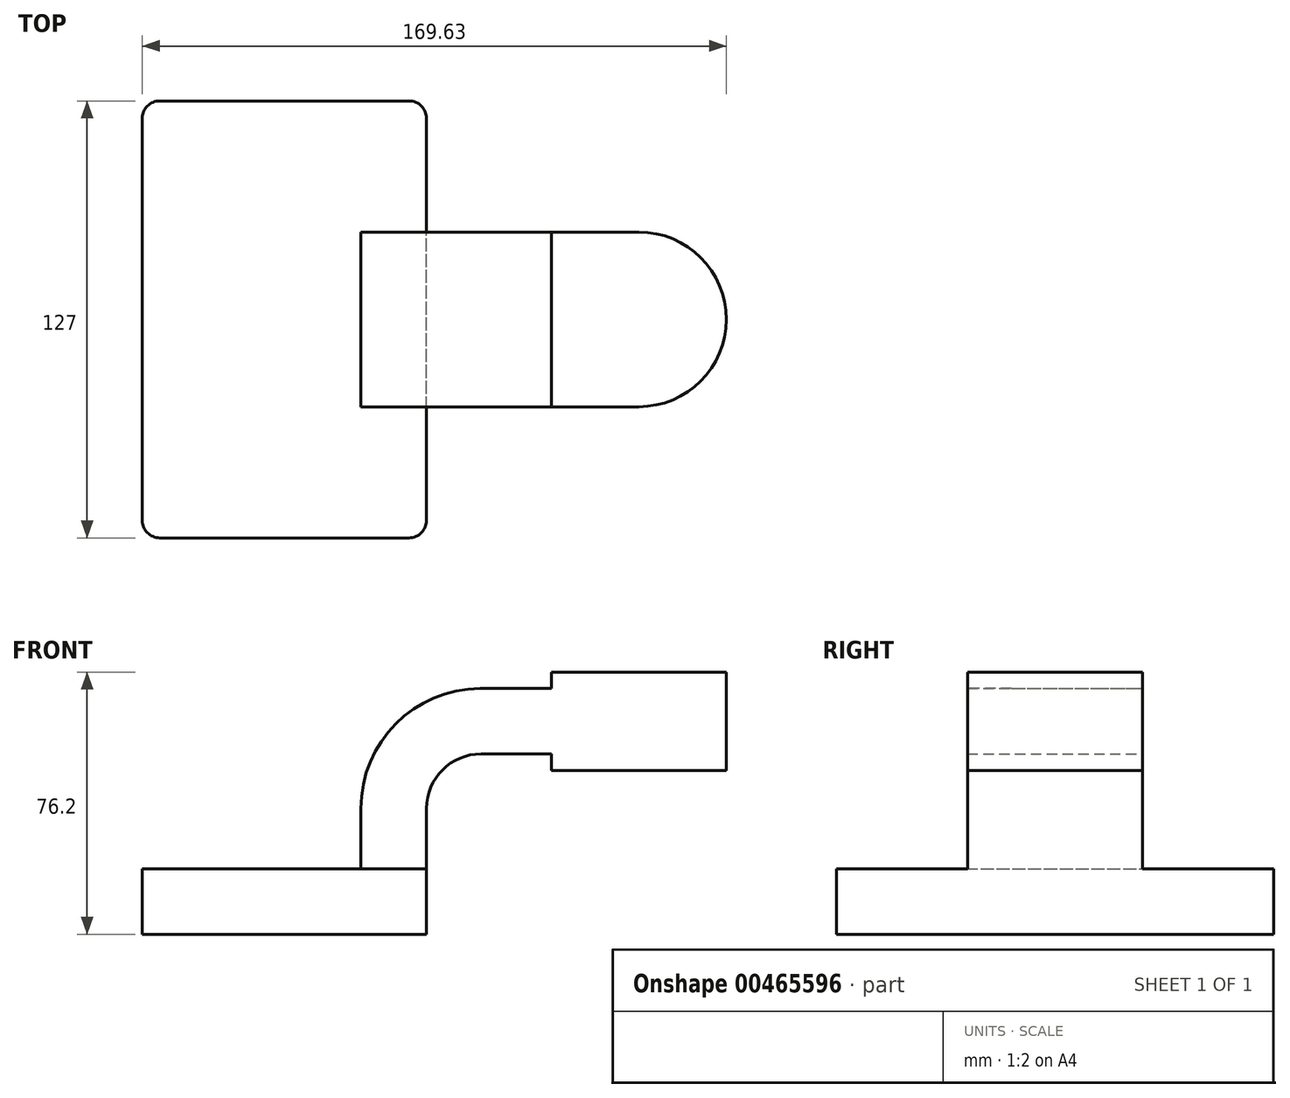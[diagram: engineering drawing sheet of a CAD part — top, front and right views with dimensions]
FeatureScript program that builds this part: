
annotation { "Feature Type Name" : "Feature", "Feature Type Description" : "" }
export const myFeature = defineFeature(function(context is Context, id is Id, definition is map)
    precondition{}
    {
        {
            var Q0;
            Q0=qCreatedBy(makeId("Front.planeOp"),FACE);
            var sketch = newSketch(context, id + "F0", { "sketchPlane" : qUnion([Q0])});
            skLineSegment(sketch, "E0.bottom", {"start": v(41.27, 9.53) * mm, "end": v(-41.27, 9.53) * mm});
            skLineSegment(sketch, "E0.top", {"start": v(41.28, -9.52) * mm, "end": v(-41.27, -9.52) * mm});
            skLineSegment(sketch, "E0.left", {"start": v(41.28, 9.53) * mm, "end": v(41.28, -9.52) * mm});
            skLineSegment(sketch, "E0.right", {"start": v(-41.27, 9.53) * mm, "end": v(-41.27, -9.52) * mm});
            skPoint(sketch, "E0.middle", {"position": v(0, 0) * mm});
            skLineSegment(sketch, "E1.bottom", {"start": v(77.56, 38.1) * mm, "end": v(128.36, 38.1) * mm});
            skLineSegment(sketch, "E1.top", {"start": v(77.56, 66.68) * mm, "end": v(128.36, 66.68) * mm});
            skLineSegment(sketch, "E1.left", {"start": v(77.56, 38.1) * mm, "end": v(77.56, 66.68) * mm});
            skLineSegment(sketch, "E1.right", {"start": v(128.36, 38.1) * mm, "end": v(128.36, 66.68) * mm});
            skPoint(sketch, "E1.middle", {"position": v(102.96, 52.39) * mm});
            skLineSegment(sketch, "E2", {"start": v(41.27, 9.53) * mm, "end": v(41.27, 27) * mm});
            skArc(sketch, "E3", {"start": v(41.27, 27) * mm, "mid": v(45.92, 38.23) * mm, "end": v(57.15, 42.88) * mm});
            skLineSegment(sketch, "E4", {"start": v(57.15, 42.88) * mm, "end": v(102.96, 42.88) * mm});
            skLineSegment(sketch, "E5.0", {"start": v(57.15, 61.93) * mm, "end": v(102.96, 61.93) * mm});
            skArc(sketch, "E5.1", {"start": v(22.22, 27) * mm, "mid": v(32.45, 51.7) * mm, "end": v(57.15, 61.93) * mm});
            skLineSegment(sketch, "E5.2", {"start": v(22.22, 9.53) * mm, "end": v(22.22, 27) * mm});
            skLineSegment(sketch, "E6", {"start": v(102.96, 38.1) * mm, "end": v(102.96, 66.68) * mm});
            skFitSpline(sketch, "E7", {"points": [v(-41.27, 9.53) * mm, v(57.15, 61.93) * mm], "startDerivative": vector(-0.2, 61.68) * mm, "endDerivative": vector(120.92, 0.2) * mm});
            skSolve(sketch);
        }
        {
            var Q0;
            Q0=makeQuery(id+"F0.imprint","IMPRINT",FACE,{"disambiguationData":[TD([[makeQuery(id+"F0.imprint","IMPRINT",EDGE,{"derivedFrom":sQuery(id+"F0.wireOp",EDGE,"E0.top")}),-1.0]])]});
            extrude(context, id + "F1", {"entities" : qUnion([Q0]), "endBound" : BoundingType.SYMMETRIC, "depth" : 127 * mm});
        }
        {
            var Q0;
            {var subQ1=sQuery(id+"F0.wireOp",EDGE,"E2");Q0=makeQuery(id+"F0.imprint","IMPRINT",FACE,{"disambiguationData":[TD([[makeQuery(id+"F0.imprint","IMPRINT",EDGE,{"derivedFrom":subQ1}),1.0]])]});}
            var Q1;
            {var subQ6=sQuery(id+"F0.wireOp",EDGE,"E6");Q1=makeQuery(id+"F0.imprint","IMPRINT",FACE,{"disambiguationData":[TD([[makeQuery(id+"F0.imprint","IMPRINT",EDGE,{"derivedFrom":subQ6}),1.0]])]});}
            extrude(context, id + "F2", {"entities" : qUnion([Q0, Q1]), "operationType" : NewBodyOperationType.ADD, "endBound" : BoundingType.SYMMETRIC, "depth" : 50.8 * mm});
        }
        {
            var Q0;
            {var subQ4=sQuery(id+"F0.wireOp",EDGE,"E5.1");Q0=makeQuery(id+"F0.imprint","IMPRINT",FACE,{"disambiguationData":[TD([[makeQuery(id+"F0.imprint","IMPRINT",EDGE,{"derivedFrom":subQ4}),1.0]])]});}
            extrude(context, id + "F3", {"entities" : qUnion([Q0]), "operationType" : NewBodyOperationType.ADD, "endBound" : BoundingType.SYMMETRIC, "depth" : 25.4 * mm});
        }
        {
            var Q0;
            {var subQ0=sQuery(id+"F0.wireOp",EDGE,"E1.right");Q0=makeQuery(id+"F0.imprint","IMPRINT",FACE,{"disambiguationData":[TD([[makeQuery(id+"F0.imprint","IMPRINT",EDGE,{"derivedFrom":subQ0}),1.0]])]});}
            var Q1;
            Q1=sQuery(id+"F0.wireOp",EDGE,"E6");
            revolve(context, id + "F4", {"operationType" : NewBodyOperationType.ADD, "entities" : qUnion([Q0]), "axis" : qUnion([Q1]), "revolveType" : RevolveType.FULL});
        }
        {
            var Q0;
            Q0=makeQuery(id+"F1.opExtrude","CAP_EDGE",EDGE,{"disambiguationData":[OSD([sQuery(id+"F0.wireOp",EDGE,"E0.left")])],"isStart":false});
            var Q1;
            Q1=makeQuery(id+"F1.opExtrude","CAP_EDGE",EDGE,{"disambiguationData":[OSD([sQuery(id+"F0.wireOp",EDGE,"E0.right")])],"isStart":false});
            var Q2;
            Q2=makeQuery(id+"F1.opExtrude","CAP_EDGE",EDGE,{"disambiguationData":[OSD([sQuery(id+"F0.wireOp",EDGE,"E0.left")])],"isStart":true});
            var Q3;
            Q3=makeQuery(id+"F1.opExtrude","CAP_EDGE",EDGE,{"disambiguationData":[OSD([sQuery(id+"F0.wireOp",EDGE,"E0.right")])],"isStart":true});
            fillet(context, id + "F5", {"entities" : qUnion([Q0, Q1, Q2, Q3]), "radius" : 5.08 * mm, "tangentPropagation" : true, "allowEdgeOverflow" : false});
        }
    });
